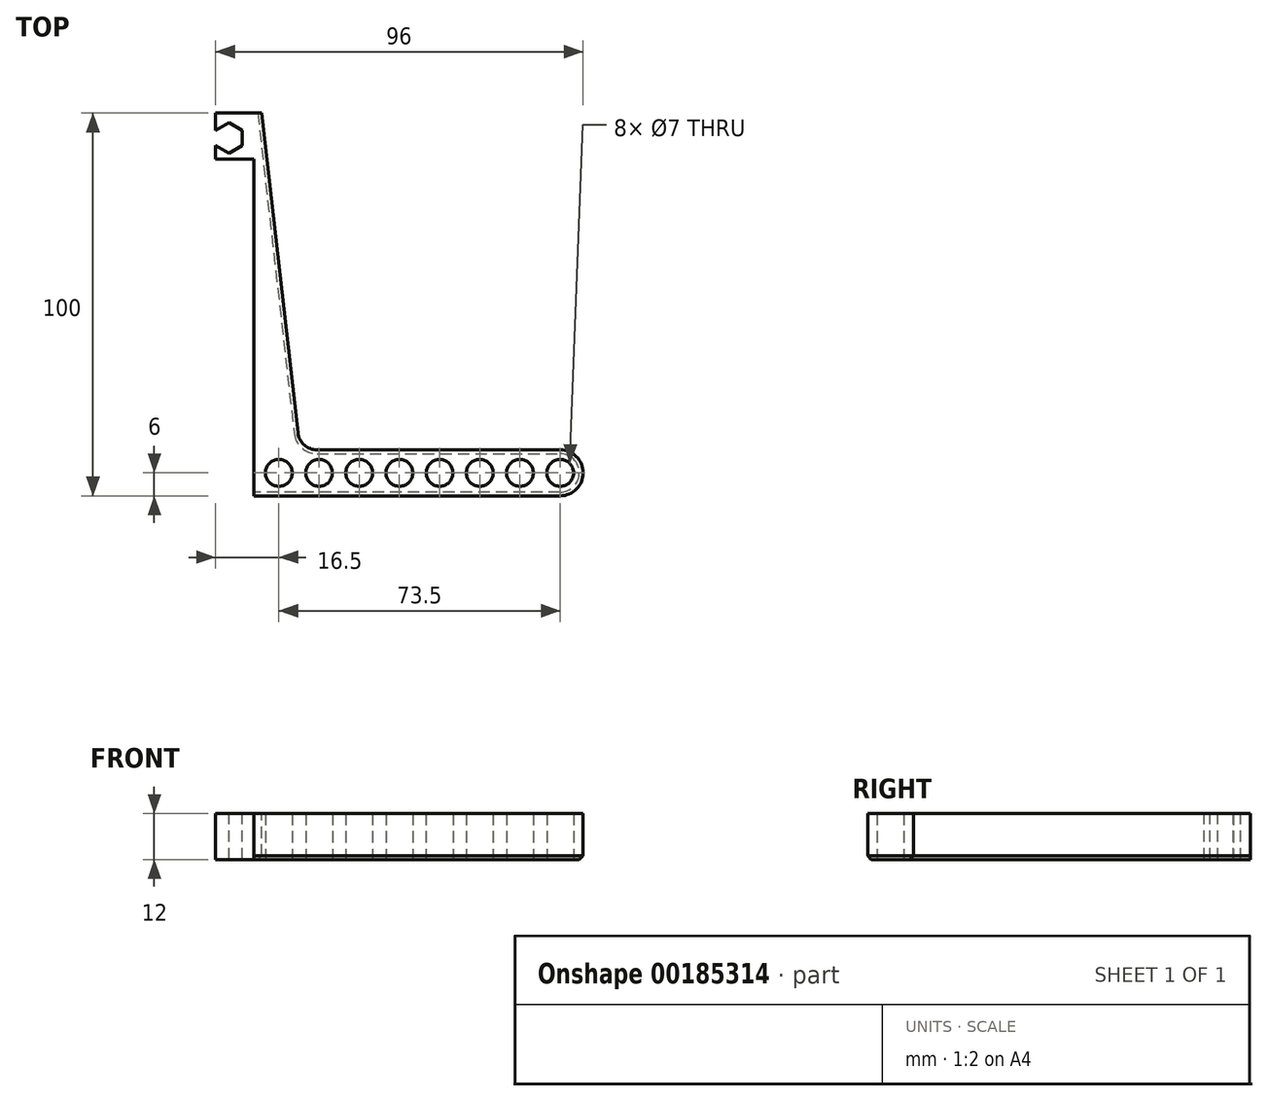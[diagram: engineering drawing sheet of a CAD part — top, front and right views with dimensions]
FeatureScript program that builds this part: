
annotation { "Feature Type Name" : "Feature", "Feature Type Description" : "" }
export const myFeature = defineFeature(function(context is Context, id is Id, definition is map)
    precondition{}
    {
        {
            var Q0;
            Q0=qCreatedBy(makeId("Top.planeOp"),FACE);
            var sketch = newSketch(context, id + "F0", { "sketchPlane" : qUnion([Q0])});
            skLineSegment(sketch, "E0.bottom", {"start": v(0, 100) * mm, "end": v(12, 100) * mm});
            skLineSegment(sketch, "E0.left", {"start": v(0, 100) * mm, "end": v(0, 0) * mm});
            skLineSegment(sketch, "E0.right", {"start": v(12, 100) * mm, "end": v(12, 12) * mm});
            skLineSegment(sketch, "E1.bottom", {"start": v(0, 0) * mm, "end": v(80, 0) * mm});
            skLineSegment(sketch, "E1.top", {"start": v(12, 12) * mm, "end": v(80, 12) * mm});
            skArc(sketch, "E2", {"start": v(80, 0) * mm, "mid": v(86, 6) * mm, "end": v(80, 12) * mm});
            skCircle(sketch, "E3.cCircle", {"center": v(80, 6) * mm, "radius": 3.5 * mm});
            skCircle(sketch, "E4.1.0.0", {"center": v(69.5, 6) * mm, "radius": 3.5 * mm});
            skCircle(sketch, "E4.2.0.0", {"center": v(59, 6) * mm, "radius": 3.5 * mm});
            skCircle(sketch, "E4.3.0.0", {"center": v(48.5, 6) * mm, "radius": 3.5 * mm});
            skCircle(sketch, "E4.4.0.0", {"center": v(38, 6) * mm, "radius": 3.5 * mm});
            skCircle(sketch, "E4.5.0.0", {"center": v(27.5, 6) * mm, "radius": 3.5 * mm});
            skCircle(sketch, "E4.6.0.0", {"center": v(17, 6) * mm, "radius": 3.5 * mm});
            skCircle(sketch, "E4.7.0.0", {"center": v(6.5, 6) * mm, "radius": 3.5 * mm});
            skLineSegment(sketch, "E4.direction1", {"start": v(80, 6) * mm, "end": v(69.5, 6) * mm, "construction": true});
            skSolve(sketch);
        }
        {
            var Q0;
            Q0=qSketchRegion(id+"F0",true);
            extrude(context, id + "F1", {"entities" : qUnion([Q0]), "depth" : 12 * mm});
        }
        {
            var Q0;
            Q0=makeQuery(id+"F1.opExtrude","CAP_FACE",FACE,{"disambiguationData":[OSD([sQuery(id+"F0.wireOp",EDGE,"E0.bottom"),sQuery(id+"F0.wireOp",EDGE,"E0.left"),sQuery(id+"F0.wireOp",EDGE,"E0.right"),sQuery(id+"F0.wireOp",EDGE,"E1.bottom"),sQuery(id+"F0.wireOp",EDGE,"E1.top"),sQuery(id+"F0.wireOp",EDGE,"E2"),sQuery(id+"F0.wireOp",EDGE,"E3.0"),sQuery(id+"F0.wireOp",EDGE,"E3.1"),sQuery(id+"F0.wireOp",EDGE,"E3.2"),sQuery(id+"F0.wireOp",EDGE,"E3.3"),sQuery(id+"F0.wireOp",EDGE,"E3.4"),sQuery(id+"F0.wireOp",EDGE,"E3.5"),sQuery(id+"F0.wireOp",EDGE,"ffaec4ea-79df-4dc1-b443-eba8a6825352.1.0.0"),sQuery(id+"F0.wireOp",EDGE,"ffaec4ea-79df-4dc1-b443-eba8a6825352.1.0.1"),sQuery(id+"F0.wireOp",EDGE,"ffaec4ea-79df-4dc1-b443-eba8a6825352.1.0.2"),sQuery(id+"F0.wireOp",EDGE,"ffaec4ea-79df-4dc1-b443-eba8a6825352.1.0.3"),sQuery(id+"F0.wireOp",EDGE,"ffaec4ea-79df-4dc1-b443-eba8a6825352.1.0.4"),sQuery(id+"F0.wireOp",EDGE,"ffaec4ea-79df-4dc1-b443-eba8a6825352.1.0.5"),sQuery(id+"F0.wireOp",EDGE,"ffaec4ea-79df-4dc1-b443-eba8a6825352.2.0.0"),sQuery(id+"F0.wireOp",EDGE,"ffaec4ea-79df-4dc1-b443-eba8a6825352.2.0.1"),sQuery(id+"F0.wireOp",EDGE,"ffaec4ea-79df-4dc1-b443-eba8a6825352.2.0.2"),sQuery(id+"F0.wireOp",EDGE,"ffaec4ea-79df-4dc1-b443-eba8a6825352.2.0.3"),sQuery(id+"F0.wireOp",EDGE,"ffaec4ea-79df-4dc1-b443-eba8a6825352.2.0.4"),sQuery(id+"F0.wireOp",EDGE,"ffaec4ea-79df-4dc1-b443-eba8a6825352.2.0.5"),sQuery(id+"F0.wireOp",EDGE,"ffaec4ea-79df-4dc1-b443-eba8a6825352.3.0.0"),sQuery(id+"F0.wireOp",EDGE,"ffaec4ea-79df-4dc1-b443-eba8a6825352.3.0.1"),sQuery(id+"F0.wireOp",EDGE,"ffaec4ea-79df-4dc1-b443-eba8a6825352.3.0.2"),sQuery(id+"F0.wireOp",EDGE,"ffaec4ea-79df-4dc1-b443-eba8a6825352.3.0.3"),sQuery(id+"F0.wireOp",EDGE,"ffaec4ea-79df-4dc1-b443-eba8a6825352.3.0.4"),sQuery(id+"F0.wireOp",EDGE,"ffaec4ea-79df-4dc1-b443-eba8a6825352.3.0.5"),sQuery(id+"F0.wireOp",EDGE,"ffaec4ea-79df-4dc1-b443-eba8a6825352.4.0.0"),sQuery(id+"F0.wireOp",EDGE,"ffaec4ea-79df-4dc1-b443-eba8a6825352.4.0.1"),sQuery(id+"F0.wireOp",EDGE,"ffaec4ea-79df-4dc1-b443-eba8a6825352.4.0.2"),sQuery(id+"F0.wireOp",EDGE,"ffaec4ea-79df-4dc1-b443-eba8a6825352.4.0.3"),sQuery(id+"F0.wireOp",EDGE,"ffaec4ea-79df-4dc1-b443-eba8a6825352.4.0.4"),sQuery(id+"F0.wireOp",EDGE,"ffaec4ea-79df-4dc1-b443-eba8a6825352.4.0.5"),sQuery(id+"F0.wireOp",EDGE,"ffaec4ea-79df-4dc1-b443-eba8a6825352.5.0.0"),sQuery(id+"F0.wireOp",EDGE,"ffaec4ea-79df-4dc1-b443-eba8a6825352.5.0.1"),sQuery(id+"F0.wireOp",EDGE,"ffaec4ea-79df-4dc1-b443-eba8a6825352.5.0.2"),sQuery(id+"F0.wireOp",EDGE,"ffaec4ea-79df-4dc1-b443-eba8a6825352.5.0.3"),sQuery(id+"F0.wireOp",EDGE,"ffaec4ea-79df-4dc1-b443-eba8a6825352.5.0.4"),sQuery(id+"F0.wireOp",EDGE,"ffaec4ea-79df-4dc1-b443-eba8a6825352.5.0.5"),sQuery(id+"F0.wireOp",EDGE,"ffaec4ea-79df-4dc1-b443-eba8a6825352.6.0.0"),sQuery(id+"F0.wireOp",EDGE,"ffaec4ea-79df-4dc1-b443-eba8a6825352.6.0.1"),sQuery(id+"F0.wireOp",EDGE,"ffaec4ea-79df-4dc1-b443-eba8a6825352.6.0.2"),sQuery(id+"F0.wireOp",EDGE,"ffaec4ea-79df-4dc1-b443-eba8a6825352.6.0.3"),sQuery(id+"F0.wireOp",EDGE,"ffaec4ea-79df-4dc1-b443-eba8a6825352.6.0.4"),sQuery(id+"F0.wireOp",EDGE,"ffaec4ea-79df-4dc1-b443-eba8a6825352.6.0.5"),sQuery(id+"F0.wireOp",EDGE,"ffaec4ea-79df-4dc1-b443-eba8a6825352.7.0.0"),sQuery(id+"F0.wireOp",EDGE,"ffaec4ea-79df-4dc1-b443-eba8a6825352.7.0.1"),sQuery(id+"F0.wireOp",EDGE,"ffaec4ea-79df-4dc1-b443-eba8a6825352.7.0.2"),sQuery(id+"F0.wireOp",EDGE,"ffaec4ea-79df-4dc1-b443-eba8a6825352.7.0.3"),sQuery(id+"F0.wireOp",EDGE,"ffaec4ea-79df-4dc1-b443-eba8a6825352.7.0.4"),sQuery(id+"F0.wireOp",EDGE,"ffaec4ea-79df-4dc1-b443-eba8a6825352.7.0.5")])],"isStart":false});
            var sketch = newSketch(context, id + "F2", { "sketchPlane" : qUnion([Q0])});
            skLineSegment(sketch, "E5", {"start": v(12, 12) * mm, "end": v(2, 100) * mm});
            skLineSegment(sketch, "E6", {"start": v(12, 12) * mm, "end": v(12, 100) * mm});
            skLineSegment(sketch, "E7", {"start": v(12, 100) * mm, "end": v(2, 100) * mm});
            skSolve(sketch);
        }
        {
            var Q0;
            Q0=qSketchRegion(id+"F2",true);
            extrude(context, id + "F3", {"entities" : qUnion([Q0]), "operationType" : NewBodyOperationType.REMOVE, "oppositeDirection" : true, "depth" : 25 * mm});
        }
        {
            var Q0;
            {var subQ0=sQuery(id+"F0.wireOp",EDGE,"E1.top");Q0=makeQuery(id+"F3.boolean.opBoolean","MERGE",EDGE,{"derivedFrom":[makeQuery(id+"F1.opExtrude","SWEPT_EDGE",EDGE,{"disambiguationData":[OSD([sQuery(id+"F0.wireOp",EDGE,"E0.right"),subQ0])]}),makeQuery(id+"F3.opExtrude","SWEPT_EDGE",EDGE,{"disambiguationData":[OSD([subQ0,sQuery(id+"F2.wireOp",EDGE,"E5"),sQuery(id+"F2.wireOp",EDGE,"E6")])]})]});}
            fillet(context, id + "F4", {"entities" : qUnion([Q0]), "radius" : 5 * mm, "tangentPropagation" : true, "allowEdgeOverflow" : false});
        }
        {
            var Q0;
            Q0=makeQuery(id+"F1.opExtrude","SWEPT_FACE",FACE,{"disambiguationData":[OSD([sQuery(id+"F0.wireOp",EDGE,"E0.left")])]});
            var sketch = newSketch(context, id + "F5", { "sketchPlane" : qUnion([Q0])});
            skLineSegment(sketch, "E8.bottom", {"start": v(-100, 0) * mm, "end": v(-88, 0) * mm});
            skLineSegment(sketch, "E8.top", {"start": v(-100, 12) * mm, "end": v(-88, 12) * mm});
            skLineSegment(sketch, "E8.left", {"start": v(-100, 0) * mm, "end": v(-100, 12) * mm});
            skLineSegment(sketch, "E8.right", {"start": v(-88, 0) * mm, "end": v(-88, 12) * mm});
            skSolve(sketch);
        }
        {
            var Q0;
            Q0=qSketchRegion(id+"F5",true);
            extrude(context, id + "F6", {"entities" : qUnion([Q0]), "operationType" : NewBodyOperationType.ADD, "depth" : 10 * mm});
        }
        {
            var Q0;
            Q0=makeQuery(id+"F6.boolean.opBoolean","MERGE",FACE,{"derivedFrom":[makeQuery(id+"F1.opExtrude","CAP_FACE",FACE,{"disambiguationData":[OSD([sQuery(id+"F0.wireOp",EDGE,"E0.bottom"),sQuery(id+"F0.wireOp",EDGE,"E0.left"),sQuery(id+"F0.wireOp",EDGE,"E0.right"),sQuery(id+"F0.wireOp",EDGE,"E1.bottom"),sQuery(id+"F0.wireOp",EDGE,"E1.top"),sQuery(id+"F0.wireOp",EDGE,"E2"),sQuery(id+"F0.wireOp",EDGE,"E3.cCircle"),sQuery(id+"F0.wireOp",EDGE,"E4.1.0.0"),sQuery(id+"F0.wireOp",EDGE,"E4.2.0.0"),sQuery(id+"F0.wireOp",EDGE,"E4.3.0.0"),sQuery(id+"F0.wireOp",EDGE,"E4.4.0.0"),sQuery(id+"F0.wireOp",EDGE,"E4.5.0.0"),sQuery(id+"F0.wireOp",EDGE,"E4.6.0.0"),sQuery(id+"F0.wireOp",EDGE,"E4.7.0.0")])],"isStart":false}),makeQuery(id+"F6.opExtrude","SWEPT_FACE",FACE,{"disambiguationData":[OSD([sQuery(id+"F5.wireOp",EDGE,"E8.top")])]})]});
            var sketch = newSketch(context, id + "F7", { "sketchPlane" : qUnion([Q0])});
            skCircle(sketch, "E9.cCircle", {"center": v(143.7, 93.5) * mm, "radius": 6.93 * mm, "construction": true});
            skPoint(sketch, "E9.cCircle.perimeterSnap0", {"position": v(-9, 93.5) * mm});
            skLineSegment(sketch, "E9.0", {"start": v(150.63, 97.5) * mm, "end": v(150.63, 89.5) * mm});
            skLineSegment(sketch, "E9.1", {"start": v(150.63, 89.5) * mm, "end": v(143.7, 85.5) * mm});
            skLineSegment(sketch, "E9.2", {"start": v(143.7, 85.5) * mm, "end": v(136.77, 89.5) * mm});
            skLineSegment(sketch, "E9.3", {"start": v(136.77, 89.5) * mm, "end": v(136.77, 97.5) * mm});
            skLineSegment(sketch, "E9.4", {"start": v(136.77, 97.5) * mm, "end": v(143.7, 101.5) * mm});
            skLineSegment(sketch, "E9.5", {"start": v(143.7, 101.5) * mm, "end": v(150.63, 97.5) * mm});
            skPoint(sketch, "E9.0.midPoint", {"position": v(150.63, 93.5) * mm});
            skPoint(sketch, "E9.0.midPoint.positionSnap0", {"position": v(-14.8, 93.5) * mm});
            skCircle(sketch, "E10.cCircle", {"center": v(-6.54, 93.5) * mm, "radius": 3.46 * mm, "construction": true});
            skLineSegment(sketch, "E10.0", {"start": v(-3.07, 91.5) * mm, "end": v(-6.54, 89.5) * mm});
            skLineSegment(sketch, "E10.1", {"start": v(-6.54, 89.5) * mm, "end": v(-10, 91.5) * mm});
            skLineSegment(sketch, "E10.2", {"start": v(-10, 91.5) * mm, "end": v(-10, 95.5) * mm});
            skLineSegment(sketch, "E10.3", {"start": v(-10, 95.5) * mm, "end": v(-6.54, 97.5) * mm});
            skLineSegment(sketch, "E10.4", {"start": v(-6.54, 97.5) * mm, "end": v(-3.07, 95.5) * mm});
            skLineSegment(sketch, "E10.5", {"start": v(-3.07, 95.5) * mm, "end": v(-3.07, 91.5) * mm});
            skPoint(sketch, "E10.0.midPoint", {"position": v(-4.8, 90.5) * mm});
            skSolve(sketch);
        }
        {
            var Q0;
            Q0=makeQuery(id+"F3.boolean.opBoolean","COPY",EDGE,{"derivedFrom":makeQuery(id+"F3.opExtrude","CAP_EDGE",EDGE,{"disambiguationData":[OSD([sQuery(id+"F2.wireOp",EDGE,"E5")])],"isStart":true})});
            var Q1;
            Q1=makeQuery(id+"F3.boolean.opBoolean","INTERSECT",EDGE,{"derivedFrom":[makeQuery(id+"F1.opExtrude","CAP_FACE",FACE,{"disambiguationData":[OSD([sQuery(id+"F0.wireOp",EDGE,"E0.bottom"),sQuery(id+"F0.wireOp",EDGE,"E0.left"),sQuery(id+"F0.wireOp",EDGE,"E0.right"),sQuery(id+"F0.wireOp",EDGE,"E1.bottom"),sQuery(id+"F0.wireOp",EDGE,"E1.top"),sQuery(id+"F0.wireOp",EDGE,"E2"),sQuery(id+"F0.wireOp",EDGE,"E3.cCircle"),sQuery(id+"F0.wireOp",EDGE,"E4.1.0.0"),sQuery(id+"F0.wireOp",EDGE,"E4.2.0.0"),sQuery(id+"F0.wireOp",EDGE,"E4.3.0.0"),sQuery(id+"F0.wireOp",EDGE,"E4.4.0.0"),sQuery(id+"F0.wireOp",EDGE,"E4.5.0.0"),sQuery(id+"F0.wireOp",EDGE,"E4.6.0.0"),sQuery(id+"F0.wireOp",EDGE,"E4.7.0.0")])],"isStart":true}),makeQuery(id+"F3.opExtrude","SWEPT_FACE",FACE,{"disambiguationData":[OSD([sQuery(id+"F2.wireOp",EDGE,"E5")])]})]});
            var Q2;
            Q2=makeQuery(id+"F3.boolean.opBoolean","COPY",EDGE,{"derivedFrom":makeQuery(id+"F3.opExtrude","SWEPT_EDGE",EDGE,{"disambiguationData":[OSD([sQuery(id+"F0.wireOp",EDGE,"E0.bottom"),sQuery(id+"F2.wireOp",EDGE,"E5"),sQuery(id+"F2.wireOp",EDGE,"E7")])]})});
            chamfer(context, id + "F8", {"entities" : qUnion([Q0, Q1, Q2]), "width" : 1 * mm, "tangentPropagation" : true});
        }
        {
            var Q0;
            Q0 = qSketchRegion(id + "F7", true);
            extrude(context, id + "F9", {"entities" : qUnion([Q0]), "operationType" : NewBodyOperationType.REMOVE, "oppositeDirection" : true, "depth" : 25 * mm});
        }
    });
